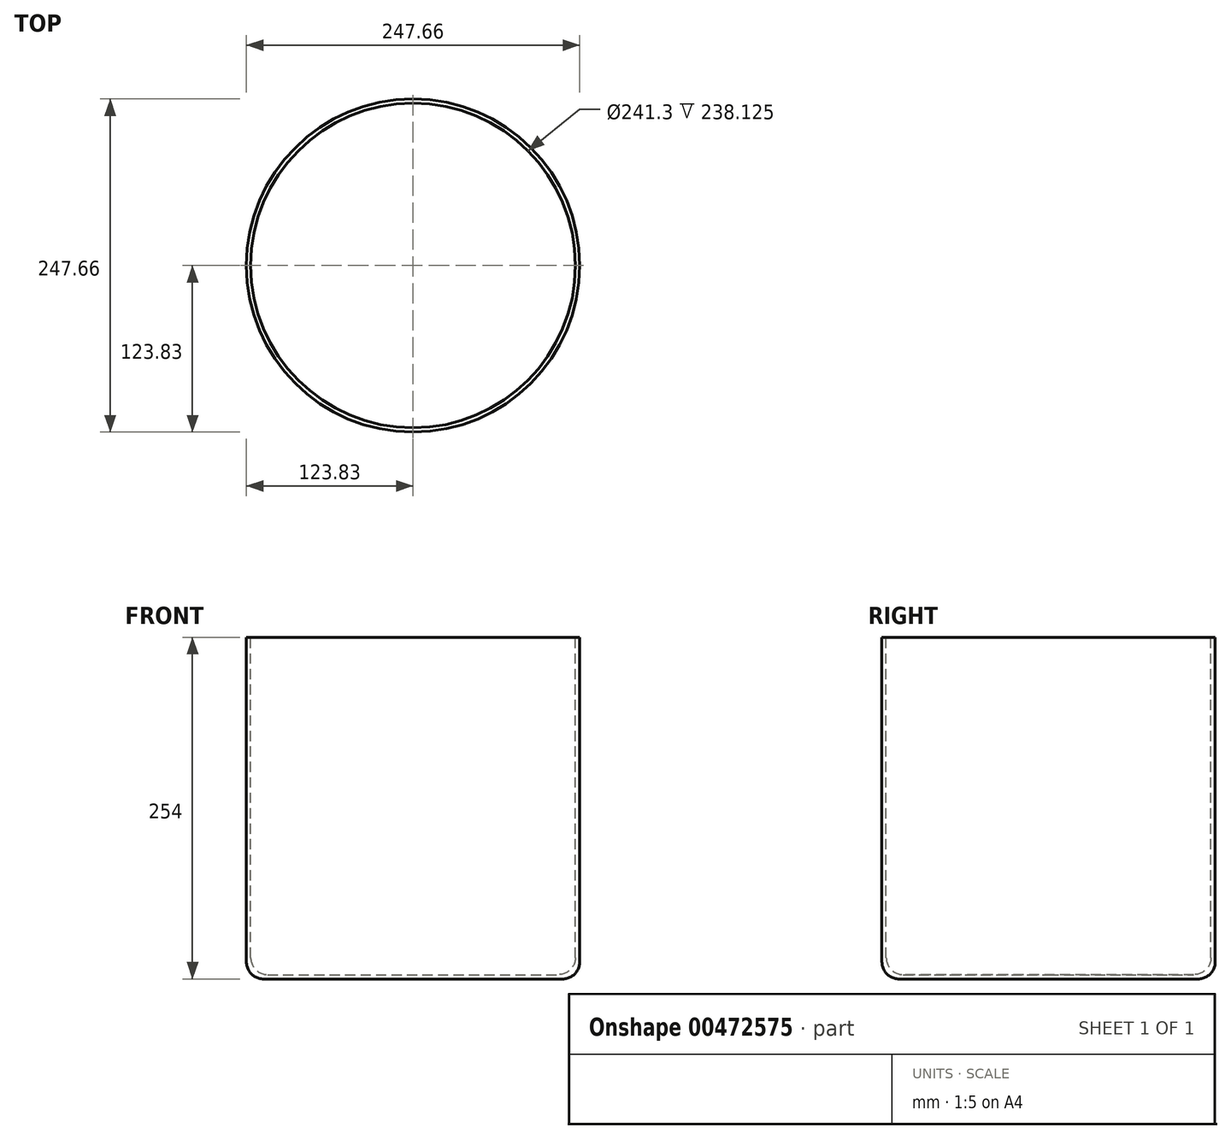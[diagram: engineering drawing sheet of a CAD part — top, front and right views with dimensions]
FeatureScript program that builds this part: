
annotation { "Feature Type Name" : "Feature", "Feature Type Description" : "" }
export const myFeature = defineFeature(function(context is Context, id is Id, definition is map)
    precondition{}
    {
        {
            var Q0;
            Q0=qCreatedBy(makeId("Top.planeOp"),FACE);
            var sketch = newSketch(context, id + "F0", { "sketchPlane" : qUnion([Q0])});
            skCircle(sketch, "E0", {"center": v(0, 0) * mm, "radius": 120.65 * mm});
            skCircle(sketch, "E1.0", {"center": v(0, 0) * mm, "radius": 123.83 * mm});
            skSolve(sketch);
        }
        {
            var Q0;
            Q0 = qSketchRegion(id + "F0", true);
            extrude(context, id + "F1", {"entities" : qUnion([Q0]), "oppositeDirection" : true, "depth" : 254 * mm});
        }
        {
            var Q0;
            Q0=makeQuery(id+"F1.opExtrude","CAP_FACE",FACE,{"disambiguationData":[OSD([sQuery(id+"F0.wireOp",EDGE,"E0"),sQuery(id+"F0.wireOp",EDGE,"E1.0")])],"isStart":false});
            var sketch = newSketch(context, id + "F2", { "sketchPlane" : qUnion([Q0])});
            skCircle(sketch, "E2.0", {"center": v(0, 0) * mm, "radius": 123.83 * mm});
            skSolve(sketch);
        }
        {
            var Q0;
            Q0 = qSketchRegion(id + "F2", true);
            extrude(context, id + "F3", {"entities" : qUnion([Q0]), "operationType" : NewBodyOperationType.ADD, "oppositeDirection" : true, "depth" : 3.17 * mm});
        }
        {
            var Q0;
            Q0=makeQuery(id+"F1.opExtrude","CAP_EDGE",EDGE,{"disambiguationData":[OSD([sQuery(id+"F0.wireOp",EDGE,"E1.0")])],"isStart":false});
            var Q1;
            Q1=makeQuery(id+"F3.opExtrude","CAP_FACE",FACE,{"disambiguationData":[OSD([sQuery(id+"F2.wireOp",EDGE,"E2.0")])],"isStart":false});
            fillet(context, id + "F4", {"entities" : qUnion([Q0, Q1]), "radius" : 12.7 * mm, "tangentPropagation" : true, "allowEdgeOverflow" : false});
        }
    });
